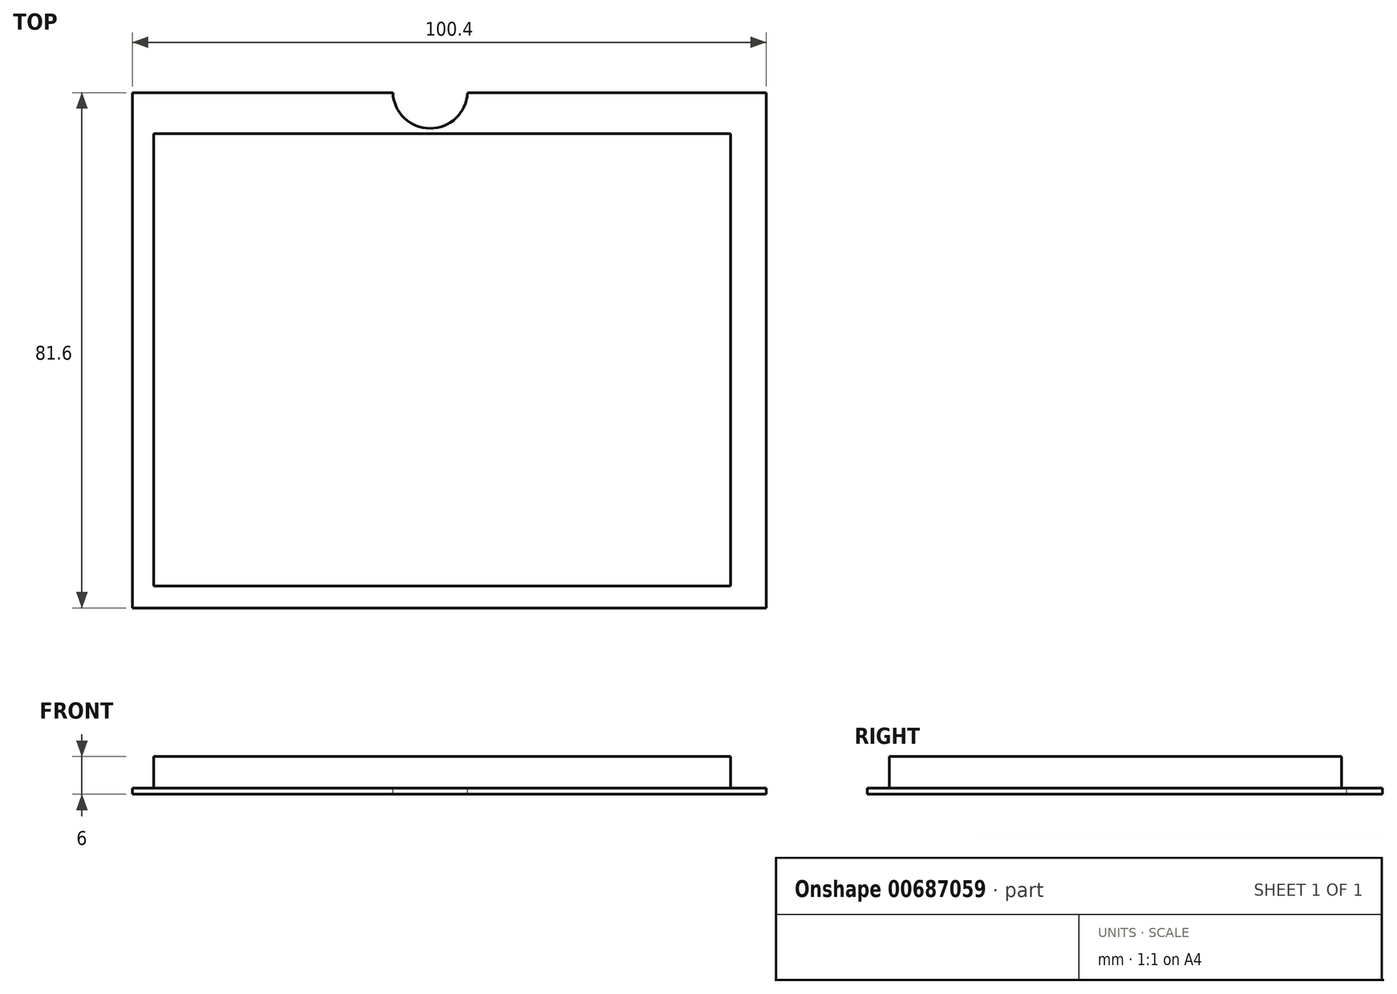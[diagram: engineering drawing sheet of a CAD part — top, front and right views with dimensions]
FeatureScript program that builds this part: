
annotation { "Feature Type Name" : "Feature", "Feature Type Description" : "" }
export const myFeature = defineFeature(function(context is Context, id is Id, definition is map)
    precondition{}
    {
        {
            var Q0;
            Q0=qCreatedBy(makeId("Top.planeOp"),FACE);
            var sketch = newSketch(context, id + "F0", { "sketchPlane" : qUnion([Q0])});
            skLineSegment(sketch, "E0.bottom", {"start": v(-47.16, -37.45) * mm, "end": v(53.24, -37.45) * mm});
            skLineSegment(sketch, "E0.top", {"start": v(-47.16, 44.15) * mm, "end": v(53.24, 44.15) * mm});
            skLineSegment(sketch, "E0.left", {"start": v(53.24, 44.15) * mm, "end": v(53.24, -37.45) * mm});
            skLineSegment(sketch, "E0.right", {"start": v(-47.16, 44.15) * mm, "end": v(-47.16, -37.45) * mm});
            skSolve(sketch);
        }
        {
            var Q0;
            Q0=makeQuery(id+"F0.imprint","IMPRINT",FACE,{"disambiguationData":[TD([[makeQuery(id+"F0.imprint","IMPRINT",EDGE,{"derivedFrom":sQuery(id+"F0.wireOp",EDGE,"E0.bottom")}),1.0]])]});
            extrude(context, id + "F1", {"entities" : qUnion([Q0]), "oppositeDirection" : true, "depth" : 1 * mm, "offsetDistance" : 25.4 * mm});
        }
        {
            var Q0;
            Q0=qCreatedBy(makeId("Top.planeOp"),FACE);
            var sketch = newSketch(context, id + "F2", { "sketchPlane" : qUnion([Q0])});
            skLineSegment(sketch, "E1.bottom", {"start": v(-43.8, 37.66) * mm, "end": v(47.6, 37.66) * mm});
            skLineSegment(sketch, "E1.top", {"start": v(-43.8, -33.94) * mm, "end": v(47.6, -33.94) * mm});
            skLineSegment(sketch, "E1.left", {"start": v(-43.8, 37.66) * mm, "end": v(-43.8, -33.94) * mm});
            skLineSegment(sketch, "E1.right", {"start": v(47.6, 37.66) * mm, "end": v(47.6, -33.94) * mm});
            skSolve(sketch);
        }
        {
            var Q0;
            Q0 = qSketchRegion(id + "F2", true);
            extrude(context, id + "F3", {"entities" : qUnion([Q0]), "operationType" : NewBodyOperationType.ADD, "depth" : 5 * mm, "offsetDistance" : 25.4 * mm});
        }
        {
            var Q0;
            Q0=qCreatedBy(makeId("Top.planeOp"),FACE);
            var sketch = newSketch(context, id + "F4", { "sketchPlane" : qUnion([Q0])});
            skCircle(sketch, "E2", {"center": v(0, 44.4) * mm, "radius": 5.92 * mm});
            skSolve(sketch);
        }
        {
            var Q0;
            Q0 = qSketchRegion(id + "F4", true);
            extrude(context, id + "F5", {"entities" : qUnion([Q0]), "operationType" : NewBodyOperationType.REMOVE, "oppositeDirection" : true, "depth" : 25.4 * mm, "offsetDistance" : 25.4 * mm});
        }
    });
